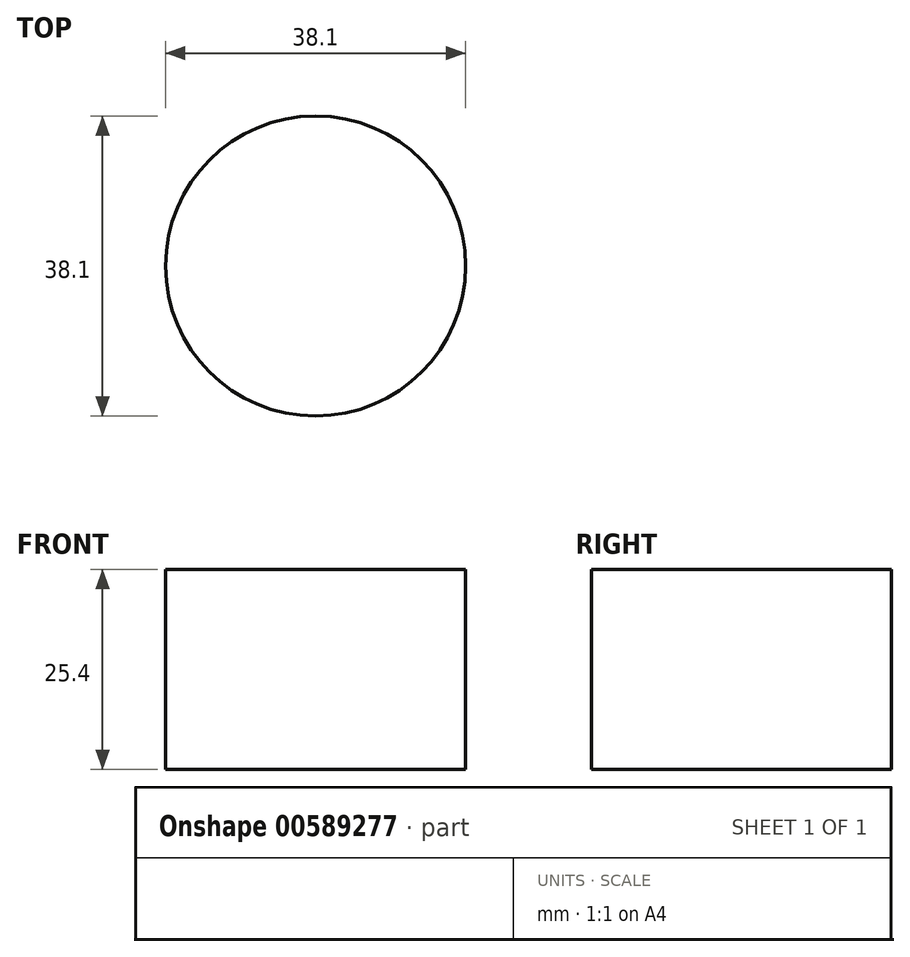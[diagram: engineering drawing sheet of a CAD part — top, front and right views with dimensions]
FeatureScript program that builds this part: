
annotation { "Feature Type Name" : "Feature", "Feature Type Description" : "" }
export const myFeature = defineFeature(function(context is Context, id is Id, definition is map)
    precondition{}
    {
        {
            var Q0;
            Q0=qCreatedBy(makeId("Top.planeOp"),FACE);
            var sketch = newSketch(context, id + "F0", { "sketchPlane" : qUnion([Q0])});
            skCircle(sketch, "E0", {"center": v(0, 0) * mm, "radius": 19.05 * mm});
            skSolve(sketch);
        }
        {
            var Q0;
            Q0 = qSketchRegion(id + "F0", true);
            extrude(context, id + "F1", {"entities" : qUnion([Q0]), "depth" : 25.4 * mm, "offsetDistance" : 25.4 * mm});
        }
    });
